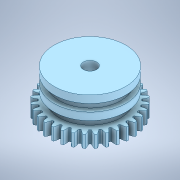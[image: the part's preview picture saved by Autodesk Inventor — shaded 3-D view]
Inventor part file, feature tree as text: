
AUTODESK INVENTOR PART (.ipt)
format: ipt  version: 2022 (Build 260153000, 153)  size: 482,816 bytes
history: native  units: in
note: dims shown in document units (in); Inventor stores cm internally (conversion verified against a paired STEP export)
features: sketch x6, extrude x4, hole x2, other x1, plane x1
ambient origin geometry x8: Origin, YZ Plane, XZ Plane, XY Plane, X Axis, Y Axis, Z Axis, Center Point
bodies: Solid1 (feature_tree)
feature tree (14):
  other  "Part 1"
  extrude  "Extrusion1"  Depth=0.1181in TaperAngle=0.0deg
  extrude  "Extrusion2"  Depth=0.1181in TaperAngle=0.0deg
  extrude  "Extrusion3"  Depth=0.1181in TaperAngle=0.0deg
  extrude  "Extrusion4"  Depth=0.1181in TaperAngle=0.0deg
  hole  "Hole1"  [1 undecoded]
  plane  "Work Plane1"
  hole  "Hole2"  [1 undecoded]
  sketch  "Sketch1"  dims[d0=0.9843in d1=0.1181in d2=0.0in]
  sketch  "Sketch2"  dims[d3=1.1417in d4=0.1181in d5=0.0in]
  sketch  "Sketch4"  dims[d7=0.9843in d8=0.1181in d9=0.0in]
  sketch  "Sketch5"  dims[d10=1.1417in d11=0.1181in d12=0.0in]
  sketch  "Sketch6"  dims[d13=0.2126in d14=0.2362in d15=0.1575in d16=0.0787in d17=90.0deg d18=0.315in d19=0.8108in d20=0.0591in]
  sketch  "Sketch7"  dims[d21=0.0591in d22=0.0591in d23=0.2362in d24=0.1575in d25=0.0787in d26=90.0deg d27=0.315in d28=0.8108in]
note: 2 required parameter values undecoded (feature->parameter linkage not recoverable at this tier; creation-order binding heuristic only, values carry confidence <= 0.55)
